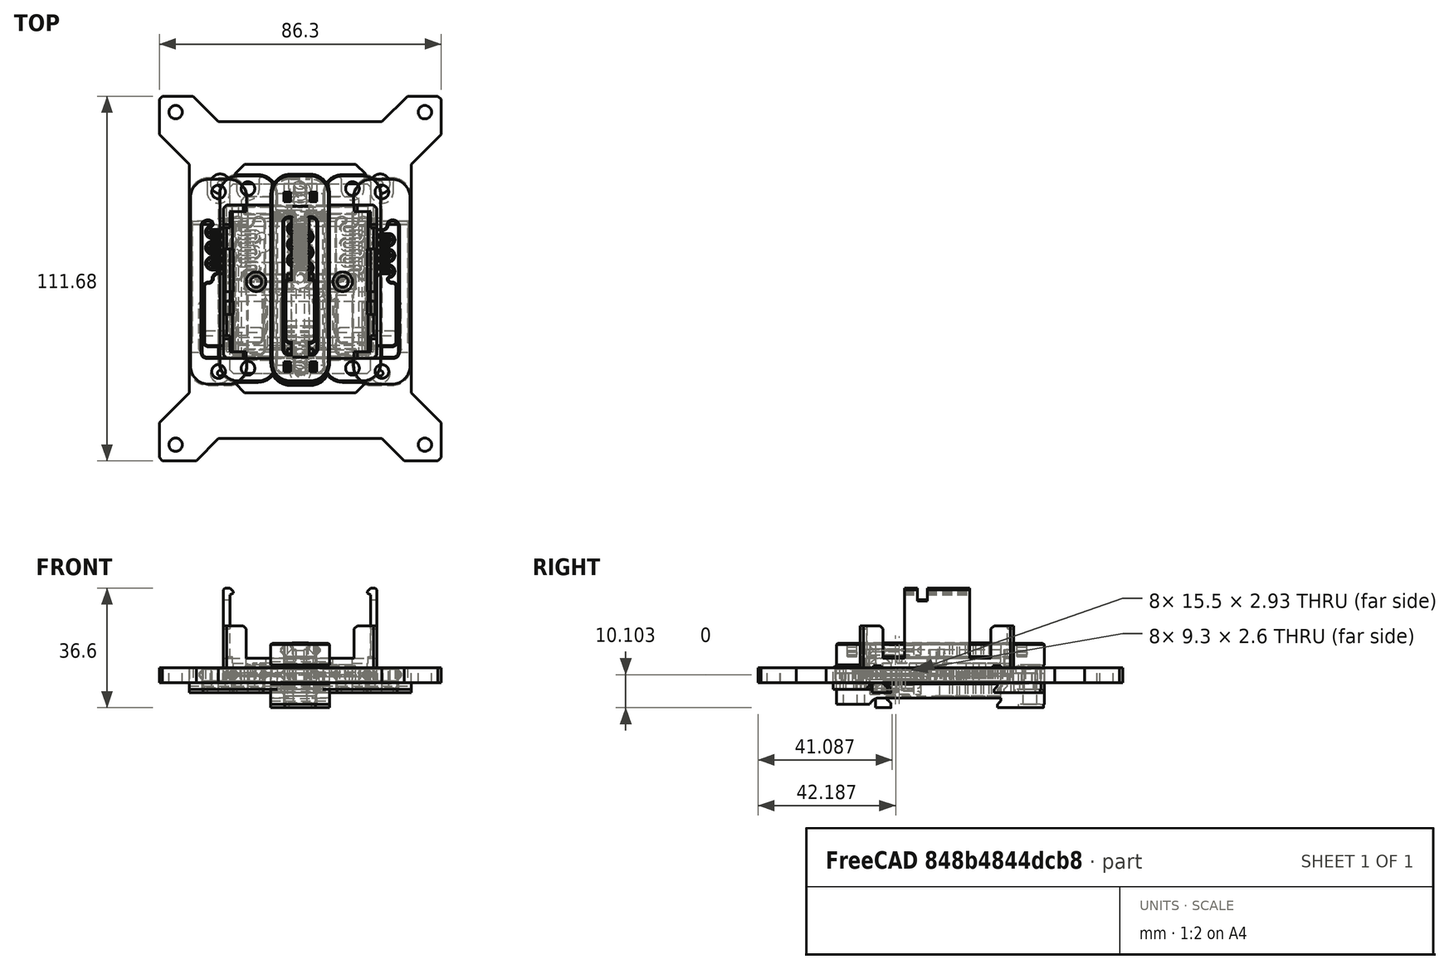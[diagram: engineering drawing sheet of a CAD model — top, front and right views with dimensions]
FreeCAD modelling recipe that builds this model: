
FCSTD DOCUMENT  (FreeCAD 0.19R24291 (Git))
Label: din-mounter
License: Other
LicenseURL: GPL3
objects: Part::Box×35, Part::Cylinder×32, Part::MultiFuse×30, Part::Cut×19, Part::Chamfer×18, Part::Feature×15, Part::Fillet×3, Sketcher::SketchObject×2, PartDesign::Pad×2, Part::MultiCommon×1, PartDesign::FeatureBase×1, PartDesign::Body×1, Part::Refine×1
note: 162 computed .brp shape members not serialized (recipe doc carries the construction recipe); baked Part::Feature solids carry a one-line shape summary decoded from their .brp

FEATURE [Part::Feature] Chamfer005007002001  label="sonoff-top "
  Placement = pos=(0,-1,7.5) rot=(0,0,1;0rad)
  shape: bbox 47 x 47 x 26.5 mm, 96 faces (baked)
FEATURE [Part::Feature] Part__Feature822  label="RS-25 PSU Bracket"
  Placement = pos=(3.35814,-1.00304,-12.0969) rot=(0,0,-1;1.5708rad)
  shape: bbox 18 x 63.6 x 7.6 mm, 163 faces (baked)
FEATURE [Part::Cylinder] Cylinder
  Angle = 360
  AttacherType = Attacher::AttachEngine3D
  Height = 6.6
  Placement = pos=(0,26.5,-6.6) rot=(0,0,1;0rad)
  Radius = 2.1
FEATURE [Part::Cylinder] Cylinder001
  Angle = 360
  AttacherType = Attacher::AttachEngine3D
  Height = 6.6
  Placement = pos=(0,-28.5,-6.6) rot=(0,0,1;0rad)
  Radius = 2.1
FEATURE [Part::MultiFuse] Fusion002
  Shapes = -> [Cylinder001,Cylinder]
FEATURE [Part::Cut] Cut  label="din-bracket-template"
  Base = -> Part__Feature822
  Placement = pos=(0,1,0) rot=(0,0,1;0rad)
  Tool = -> Fusion002
FEATURE [Part::Feature] Cut001  label="din-bracket001"
  Placement = pos=(0,1.5,4.6) rot=(0,0,1;0rad)
  shape: bbox 18 x 63.6 x 7.6 mm, 165 faces (baked)
FEATURE [Part::Box] Box  label="Cube"
  AttacherType = Attacher::AttachEngine3D
  Height = 4.6
  Length = 47
  Placement = pos=(-23.5,-24.5,0) rot=(0,0,1;0rad)
  Width = 47
FEATURE [Part::Chamfer] Chamfer
  Base = -> Box
  Edges = 4 edges r=1: [Edge1,Edge3,Edge5,Edge7]
FEATURE [Part::Chamfer] Chamfer005007002002
  Base = -> Chamfer
  Edges = 8 edges r=0.4: [Edge1,Edge5,Edge6,Edge7,Edge8,Edge9,Edge10,Edge11]
FEATURE [Part::Box] Box001  label="Cube001"
  AttacherType = Attacher::AttachEngine3D
  Height = 10
  Length = 16
  Placement = pos=(-8,-26,0) rot=(0,0,1;0rad)
  Width = 50
FEATURE [Part::Cut] Cut002
  Base = -> Chamfer005007002002
  Tool = -> Box001
FEATURE [Part::Box] Box003  label="Cube003"
  AttacherType = Attacher::AttachEngine3D
  Height = 10
  Length = 20
  Placement = pos=(-10,22.5,0) rot=(0,0,1;0rad)
  Width = 15
FEATURE [Part::Box] Box002  label="Cube002"
  AttacherType = Attacher::AttachEngine3D
  Height = 10
  Length = 20
  Placement = pos=(-10,-39.5,0) rot=(0,0,1;0rad)
  Width = 15
FEATURE [Part::MultiFuse] Fusion
  Placement = pos=(0,0,-4) rot=(0,0,1;0rad)
  Shapes = -> [Box002,Box003]
FEATURE [Part::Cut] Cut003
  Base = -> Cut001
  Tool = -> Fusion
FEATURE [Part::Chamfer] Chamfer005007002003
  Base = -> Cut003
  Edges = 2 edges r=0.4: [Edge1,Edge3]
FEATURE [Part::Chamfer] Chamfer005007002004
  Base = -> Chamfer005007002003
  Edges = 2 edges r=0.4: [Edge172,Edge174]
FEATURE [Part::MultiFuse] Fusion003
  Shapes = -> [Cut002,Chamfer005007002004]
FEATURE [Part::Cylinder] Cylinder002
  Angle = 360
  AttacherType = Attacher::AttachEngine3D
  Height = 10
  Placement = pos=(-13.5,-1,0) rot=(0,0,1;0rad)
  Radius = 2.05
FEATURE [Part::Cylinder] Cylinder003
  Angle = 360
  AttacherType = Attacher::AttachEngine3D
  Height = 10
  Placement = pos=(13,-1,0) rot=(0,0,1;0rad)
  Radius = 2.05
FEATURE [Part::MultiFuse] Fusion004
  Shapes = -> [Cylinder003,Cylinder002]
FEATURE [Part::Cut] Cut004
  Base = -> Fusion003
  Tool = -> Fusion004
FEATURE [Part::Chamfer] Chamfer005007002005  label="sonoff"
  Base = -> Cut004
  Edges = 2 edges r=0.2: [Edge19,Edge177]
FEATURE [Part::Box] Box004  label="Cube004"
  AttacherType = Attacher::AttachEngine3D
  Height = 4.6
  Length = 43
  Placement = pos=(-21.5,-29,0) rot=(0,0,1;0rad)
  Width = 58
FEATURE [Part::Cylinder] Cylinder004
  Angle = 360
  AttacherType = Attacher::AttachEngine3D
  Height = 15
  Placement = pos=(0,23.75,-6) rot=(0,0,1;0rad)
  Radius = 2.05
FEATURE [Part::Cylinder] Cylinder005
  Angle = 360
  AttacherType = Attacher::AttachEngine3D
  Height = 15
  Placement = pos=(0,-23.75,-6) rot=(0,0,1;0rad)
  Radius = 2.05
FEATURE [Part::Feature] Cut005  label="din-bracket002"
  Placement = pos=(0,3,4.6) rot=(0,0,1;0rad)
  shape: bbox 18 x 63.6 x 7.6 mm, 165 faces (baked)
FEATURE [Part::Box] Box005  label="Cube005"
  AttacherType = Attacher::AttachEngine3D
  Height = 9.6
  Length = 43
  Placement = pos=(-21.5,-29,-4) rot=(0,0,1;0rad)
  Width = 58
FEATURE [Part::MultiCommon] Common
  Shapes = -> [Box005,Cut005]
FEATURE [Part::Box] Box006  label="Cube006"
  AttacherType = Attacher::AttachEngine3D
  Height = 10
  Length = 15
  Placement = pos=(-7.5,-26.5,0) rot=(0,0,1;0rad)
  Width = 54
FEATURE [Part::Cut] Cut006
  Base = -> Box004
  Tool = -> Box006
FEATURE [Part::Box] Box007  label="Cube007"
  AttacherType = Attacher::AttachEngine3D
  Height = 6.6
  Length = 5
  Placement = pos=(-2.5,-28,-2) rot=(0,0,1;0rad)
  Width = 6
FEATURE [Part::Box] Box008  label="Cube008"
  AttacherType = Attacher::AttachEngine3D
  Height = 7.6
  Length = 10
  Placement = pos=(-5,24,-3) rot=(0,0,1;0rad)
  Width = 5
FEATURE [Part::Box] Box009  label="Cube009"
  AttacherType = Attacher::AttachEngine3D
  Height = 10
  Length = 36
  Placement = pos=(-18,-25,0) rot=(0,0,1;0rad)
  Width = 50
FEATURE [Part::MultiFuse] Fusion008
  Shapes = -> [Cylinder004,Cylinder005]
FEATURE [Part::Feature] Fusion001001  label="wago-004"
  Placement = pos=(-1,11,4.09) rot=(0,0,1;1.5708rad)
  shape: bbox 22.25 x 23.15 x 12.2 mm, 62 faces (baked)
FEATURE [Part::Feature] Fusion001002  label="wago-005"
  Placement = pos=(1,11,4.09) rot=(0,0,-1;1.5708rad)
  shape: bbox 22.25 x 23.15 x 12.2 mm, 62 faces (baked)
FEATURE [Part::Feature] Fusion001003  label="wago-006"
  Placement = pos=(1,-12,4.09) rot=(0,0,-1;1.5708rad)
  shape: bbox 22.25 x 23.15 x 12.2 mm, 62 faces (baked)
FEATURE [Part::Feature] Fusion001004  label="wago-007"
  Placement = pos=(-1,-12,4.09) rot=(0,0,1;1.5708rad)
  shape: bbox 22.25 x 23.15 x 12.2 mm, 62 faces (baked)
FEATURE [Part::MultiFuse] Fusion001005
  Placement = pos=(22,-0.5,0) rot=(0,0,1;0rad)
  Shapes = -> [Fusion001001,Fusion001004]
FEATURE [Part::MultiFuse] Fusion001006
  Placement = pos=(-22,-0.5,0) rot=(0,0,1;0rad)
  Shapes = -> [Fusion001002,Fusion001003]
FEATURE [Part::MultiFuse] Fusion001007
  Shapes = -> [Fusion001006,Fusion001005]
FEATURE [Part::Box] Box011  label="Cube011"
  AttacherType = Attacher::AttachEngine3D
  Height = 5
  Length = 18
  Placement = pos=(-9,21.8,0) rot=(0,0,1;0rad)
  Width = 9
FEATURE [Part::Box] Box012  label="Cube012"
  AttacherType = Attacher::AttachEngine3D
  Height = 5
  Length = 18
  Placement = pos=(-9,-32.8,0) rot=(0,0,1;0rad)
  Width = 9
FEATURE [Part::Fillet] Fillet
  Base = -> Box012
  Edges = 2 edges r=6: [Edge1,Edge5]
FEATURE [Part::Fillet] Fillet001
  Base = -> Box011
  Edges = 2 edges r=6: [Edge3,Edge7]
FEATURE [Part::Cylinder] Cylinder006
  Angle = 360
  AttacherType = Attacher::AttachEngine3D
  Height = 10
  Placement = pos=(0,26.5,0) rot=(0,0,1;0rad)
  Radius = 1.7
FEATURE [Part::Cylinder] Cylinder007
  Angle = 360
  AttacherType = Attacher::AttachEngine3D
  Height = 10
  Placement = pos=(0,-28.5,0) rot=(0,0,1;0rad)
  Radius = 1.7
FEATURE [Part::Cylinder] Cylinder008
  Angle = 360
  AttacherType = Attacher::AttachEngine3D
  Height = 2
  Placement = pos=(0,-28.5,0) rot=(0,0,1;0rad)
  Radius = 3.25
FEATURE [Part::Cylinder] Cylinder009
  Angle = 360
  AttacherType = Attacher::AttachEngine3D
  Height = 2
  Placement = pos=(0,26.5,0) rot=(0,0,1;0rad)
  Radius = 3.25
FEATURE [Part::MultiFuse] Fusion001008
  Shapes = -> [Cylinder007,Cylinder006]
FEATURE [Part::MultiFuse] Fusion001009
  Placement = pos=(0,0,3) rot=(0,0,1;0rad)
  Shapes = -> [Cylinder009,Cylinder008]
FEATURE [Part::MultiFuse] Fusion001010
  Shapes = -> [Fusion001009,Fusion001008]
FEATURE [Part::Chamfer] Chamfer005007002008
  Base = -> Fillet001
  Edges = 10 edges r=0.4: [Edge1,Edge4,Edge5,Edge7,Edge8,Edge9,Edge10,Edge14,Edge15,Edge16]
FEATURE [Part::Chamfer] Chamfer005007002009
  Base = -> Fillet
  Edges = 10 edges r=0.4: [Edge1,Edge4,Edge5,Edge7,Edge8,Edge9,Edge10,Edge14,Edge15,Edge16]
FEATURE [Part::MultiFuse] Fusion001011
  Shapes = -> [Chamfer005007002009,Chamfer005007002008,Fusion001007]
FEATURE [Part::Cut] Cut009  label="wago-3x4"
  Base = -> Fusion001011
  Tool = -> Fusion001010
FEATURE [Part::Chamfer] Chamfer005007002010
  Base = -> Box009
  Edges = 4 edges r=1: [Edge1,Edge3,Edge5,Edge7]
FEATURE [Part::Chamfer] Chamfer005007002011
  Base = -> Cut006
  Edges = 4 edges r=1: [Edge1,Edge3,Edge6,Edge15]
FEATURE [Part::Cut] Cut010
  Base = -> Chamfer005007002011
  Tool = -> Chamfer005007002010
FEATURE [Part::MultiFuse] Fusion001012
  Shapes = -> [Common,Box007,Box008]
FEATURE [Part::MultiFuse] Fusion001013
  Shapes = -> [Cut010,Fusion001012]
FEATURE [Part::Cut] Cut011  label="omron-ssr"
  Base = -> Fusion001013
  Tool = -> Fusion008
FEATURE [Part::Feature] Cut012  label="din-bracket-template001"
  Placement = pos=(-25,0,4.6) rot=(0,0,1;0rad)
  shape: bbox 18 x 63.6 x 7.6 mm, 165 faces (baked)
FEATURE [Part::Cylinder] Cylinder010
  Angle = 360
  AttacherType = Attacher::AttachEngine3D
  Height = 10
  Placement = pos=(38.15,50.925,0) rot=(0,0,1;0rad)
  Radius = 2.05
FEATURE [Part::Cylinder] Cylinder011
  Angle = 360
  AttacherType = Attacher::AttachEngine3D
  Height = 10
  Placement = pos=(38.15,-50.92,0) rot=(0,0,1;0rad)
  Radius = 2.05
FEATURE [Part::Cylinder] Cylinder012
  Angle = 360
  AttacherType = Attacher::AttachEngine3D
  Height = 10
  Placement = pos=(-38.15,-50.92,0) rot=(0,0,1;0rad)
  Radius = 2.05
FEATURE [Part::Cylinder] Cylinder013
  Angle = 360
  AttacherType = Attacher::AttachEngine3D
  Height = 10
  Placement = pos=(-38.15,50.925,0) rot=(0,0,1;0rad)
  Radius = 2.05
FEATURE [Part::Feature] Cut013  label="din-bracket-template002"
  Placement = pos=(25,0,4.6) rot=(0,0,1;0rad)
  shape: bbox 18 x 63.6 x 7.6 mm, 165 faces (baked)
FEATURE [Part::Box] Box013  label="Cube013"
  AttacherType = Attacher::AttachEngine3D
  Height = 4.6
  Length = 86.3
  Placement = pos=(-43.15,-55.835,0) rot=(0,0,1;0rad)
  Width = 111.67
FEATURE [Part::Box] Box014  label="Cube014"
  AttacherType = Attacher::AttachEngine3D
  Height = 10
  Length = 16
  Placement = pos=(-33,-24.5,0) rot=(0,0,1;0rad)
  Width = 44
FEATURE [Part::Box] Box015  label="Cube015"
  AttacherType = Attacher::AttachEngine3D
  Height = 10
  Length = 16
  Placement = pos=(17,-24.5,0) rot=(0,0,1;0rad)
  Width = 44
FEATURE [Part::MultiFuse] Fusion001014
  Shapes = -> [Box015,Box014]
FEATURE [Part::Cut] Cut014
  Base = -> Box013
  Tool = -> Fusion001014
FEATURE [Part::MultiFuse] Fusion001015
  Shapes = -> [Cylinder010,Cylinder011,Cylinder013,Cylinder012]
FEATURE [Part::Chamfer] Chamfer005007002012
  Base = -> Cut014
  Edges = 4 edges r=1: [Edge1,Edge3,Edge6,Edge19]
FEATURE [Part::Cut] Cut015
  Base = -> Chamfer005007002012
  Tool = -> Fusion001015
FEATURE [Part::Box] Box016  label="Cube016"
  AttacherType = Attacher::AttachEngine3D
  Height = 10
  Length = 40
  Placement = pos=(-20,-35,0) rot=(0,0,1;0rad)
  Width = 70
FEATURE [Part::Box] Box017  label="Cube017"
  AttacherType = Attacher::AttachEngine3D
  Height = 10
  Length = 70
  Placement = pos=(-35,-60,0) rot=(0,0,1;0rad)
  Width = 26
FEATURE [Part::Box] Box018  label="Cube018"
  AttacherType = Attacher::AttachEngine3D
  Height = 10
  Length = 70
  Placement = pos=(-35,55,0) rot=(0,0,1;0rad)
  Width = 26
FEATURE [Part::Chamfer] Chamfer005007002013
  Base = -> Box018
  Edges = 2 edges r=10: [Edge1,Edge5]
  Placement = pos=(0,-7,0) rot=(0,0,1;0rad)
FEATURE [Part::Chamfer] Chamfer005007002014
  Base = -> Box017
  Edges = 2 edges r=10: [Edge3,Edge7]
  Placement = pos=(0,-15,0) rot=(0,0,1;0rad)
FEATURE [Part::Chamfer] Chamfer005007002015
  Base = -> Box016
  Edges = 4 edges r=3: [Edge1,Edge3,Edge5,Edge7]
FEATURE [Part::Box] Box019  label="Cube019"
  AttacherType = Attacher::AttachEngine3D
  Height = 10
  Length = 40
  Placement = pos=(-75,-45,0) rot=(0,0,1;0rad)
  Width = 90
FEATURE [Part::Box] Box020  label="Cube020"
  AttacherType = Attacher::AttachEngine3D
  Height = 10
  Length = 40
  Placement = pos=(40,-45,0) rot=(0,0,1;0rad)
  Width = 90
FEATURE [Part::Chamfer] Chamfer005007002016
  Base = -> Box019
  Edges = 2 edges r=10: [Edge5,Edge7]
  Placement = pos=(1,0,0) rot=(0,0,1;0rad)
FEATURE [Part::Chamfer] Chamfer005007002017
  Base = -> Box020
  Edges = 2 edges r=10: [Edge1,Edge3]
  Placement = pos=(-6,0,0) rot=(0,0,1;0rad)
FEATURE [Part::MultiFuse] Fusion001016
  Shapes = -> [Chamfer005007002016,Chamfer005007002017,Chamfer005007002015,Chamfer005007002014,Chamfer005007002013]
FEATURE [Part::Box] Box021  label="Cube021"
  AttacherType = Attacher::AttachEngine3D
  Height = 4.6
  Length = 33
  Placement = pos=(-16.5,-5,0) rot=(0,0,1;0rad)
  Width = 10
FEATURE [Part::Cut] Cut016
  Base = -> Cut015
  Tool = -> Fusion001016
FEATURE [Part::MultiFuse] Fusion001017  label="skr-13_14"
  Shapes = -> [Cut016,Box021,Cut012,Cut013]
FEATURE [Part::Feature] Cut017  label="din-bracket-template003"
  Placement = pos=(-16,1,4.6) rot=(0,0,1;0rad)
  shape: bbox 18 x 63.6 x 7.6 mm, 165 faces (baked)
FEATURE [Part::Cylinder] Cylinder014
  Angle = 360
  AttacherType = Attacher::AttachEngine3D
  Height = 4.6
  Placement = pos=(24.5,29,0) rot=(0,0,1;0rad)
  Radius = 3
FEATURE [Part::Cylinder] Cylinder015
  Angle = 360
  AttacherType = Attacher::AttachEngine3D
  Height = 4.6
  Placement = pos=(24.5,-29,0) rot=(0,0,1;0rad)
  Radius = 3
FEATURE [Part::Cylinder] Cylinder016
  Angle = 360
  AttacherType = Attacher::AttachEngine3D
  Height = 4.6
  Placement = pos=(-24.5,-29,0) rot=(0,0,1;0rad)
  Radius = 3
FEATURE [Part::Cylinder] Cylinder017
  Angle = 360
  AttacherType = Attacher::AttachEngine3D
  Height = 4.6
  Placement = pos=(-24.5,29,0) rot=(0,0,1;0rad)
  Radius = 3
FEATURE [Part::Feature] Cut018  label="din-bracket-template004"
  Placement = pos=(16,1,4.6) rot=(0,0,1;0rad)
  shape: bbox 18 x 63.6 x 7.6 mm, 165 faces (baked)
FEATURE [Part::Cylinder] Cylinder018
  Angle = 360
  AttacherType = Attacher::AttachEngine3D
  Height = 4.6
  Placement = pos=(-24.5,29,0) rot=(0,0,1;0rad)
  Radius = 0.85
FEATURE [Part::Cylinder] Cylinder019
  Angle = 360
  AttacherType = Attacher::AttachEngine3D
  Height = 4.6
  Placement = pos=(24.5,29,0) rot=(0,0,1;0rad)
  Radius = 0.85
FEATURE [Part::Cylinder] Cylinder020
  Angle = 360
  AttacherType = Attacher::AttachEngine3D
  Height = 4.6
  Placement = pos=(24.5,-29,0) rot=(0,0,1;0rad)
  Radius = 0.85
FEATURE [Part::Cylinder] Cylinder021
  Angle = 360
  AttacherType = Attacher::AttachEngine3D
  Height = 4.6
  Placement = pos=(-24.5,-29,0) rot=(0,0,1;0rad)
  Radius = 0.85
FEATURE [Part::MultiFuse] Fusion001018
  Shapes = -> [Cylinder021,Cylinder020,Cylinder019,Cylinder018]
FEATURE [Part::MultiFuse] Fusion001019
  Shapes = -> [Cylinder017,Cylinder014,Cylinder015,Cylinder016]
FEATURE [Part::Box] Box022  label="Cube022"
  AttacherType = Attacher::AttachEngine3D
  Height = 4.6
  Length = 15
  Placement = pos=(-7.5,-26.5,0) rot=(0,0,1;0rad)
  Width = 5
FEATURE [Part::Box] Box023  label="Cube023"
  AttacherType = Attacher::AttachEngine3D
  Height = 4.6
  Length = 15
  Placement = pos=(-7.5,21,0) rot=(0,0,1;0rad)
  Width = 5
FEATURE [Part::MultiFuse] Fusion001020
  Shapes = -> [Box023,Box022,Cut018,Cut017,Fusion001019]
FEATURE [Part::Cut] Cut019  label="pi"
  Base = -> Fusion001020
  Tool = -> Fusion001018
FEATURE [Part::Cylinder] Cylinder022
  Angle = 360
  AttacherType = Attacher::AttachEngine3D
  Height = 4
  Radius = 3
FEATURE [Part::Cylinder] Cylinder023
  Angle = 360
  AttacherType = Attacher::AttachEngine3D
  Height = 4
  Radius = 1.2
FEATURE [Part::Cut] Cut020  label="m2-washer"
  Base = -> Cylinder022
  Tool = -> Cylinder023
FEATURE [Part::Cylinder] Cylinder024
  Angle = 360
  AttacherType = Attacher::AttachEngine3D
  Height = 4
  Radius = 3.5
FEATURE [Part::Cylinder] Cylinder025
  Angle = 360
  AttacherType = Attacher::AttachEngine3D
  Height = 10
  Radius = 1.7
FEATURE [Part::Cut] Cut021  label="m3-washer"
  Base = -> Cylinder024
  Tool = -> Cylinder025
FEATURE [Part::Box] Box024  label="Cube024"
  AttacherType = Attacher::AttachEngine3D
  Height = 8
  Length = 45
  Placement = pos=(-22.5,-22.5,0) rot=(0,0,1;0rad)
  Width = 45
FEATURE [Part::Box] Box025  label="Cube025"
  AttacherType = Attacher::AttachEngine3D
  Height = 6
  Length = 41
  Placement = pos=(-20.5,-22.5,3) rot=(0,0,1;0rad)
  Width = 45
FEATURE [Part::Cylinder] Cylinder026
  Angle = 360
  AttacherType = Attacher::AttachEngine3D
  Height = 6
  Placement = pos=(-11.5,11,0) rot=(0,0,1;0rad)
  Radius = 0.85
FEATURE [Part::Cylinder] Cylinder027
  Angle = 360
  AttacherType = Attacher::AttachEngine3D
  Height = 6
  Placement = pos=(6.645,-6.415,0) rot=(0,0,1;0rad)
  Radius = 0.85
FEATURE [Part::Box] Box026  label="Cube026"
  AttacherType = Attacher::AttachEngine3D
  Height = 3
  Length = 18
  Placement = pos=(-9,22.5,0) rot=(0,0,1;0rad)
  Width = 9.4
FEATURE [Part::Box] Box027  label="Cube027"
  AttacherType = Attacher::AttachEngine3D
  Height = 3
  Length = 18
  Placement = pos=(-9,-31.9,0) rot=(0,0,1;0rad)
  Width = 9.4
FEATURE [Part::MultiFuse] Fusion001021
  Shapes = -> [Box027,Box026]
FEATURE [Part::Fillet] Fillet002
  Base = -> Fusion001021
  Edges = 4 edges r=6: [Edge1,Edge5,Edge15,Edge19]
FEATURE [Part::MultiFuse] Fusion001022
  Shapes = -> [Box024,Fillet002]
FEATURE [Part::Cut] Cut022
  Base = -> Fusion001022
  Tool = -> Box025
FEATURE [Part::Cylinder] Cylinder028
  Angle = 360
  AttacherType = Attacher::AttachEngine3D
  Height = 6
  Placement = pos=(-11.5,11,0) rot=(0,0,1;0rad)
  Radius = 3
FEATURE [Part::Cylinder] Cylinder029
  Angle = 360
  AttacherType = Attacher::AttachEngine3D
  Height = 6
  Placement = pos=(6.645,-6.415,0) rot=(0,0,1;0rad)
  Radius = 3
FEATURE [Part::Cylinder] Cylinder030
  Angle = 360
  AttacherType = Attacher::AttachEngine3D
  Height = 10
  Placement = pos=(0,27.5,0) rot=(0,0,1;0rad)
  Radius = 1.7
FEATURE [Part::Cylinder] Cylinder031
  Angle = 360
  AttacherType = Attacher::AttachEngine3D
  Height = 10
  Placement = pos=(0,-27.5,0) rot=(0,0,1;0rad)
  Radius = 1.7
FEATURE [Part::MultiFuse] Fusion001026
  Shapes = -> [Cylinder031,Cylinder030]
FEATURE [Part::Cut] Cut023
  Base = -> Cut022
  Tool = -> Fusion001026
FEATURE [Part::Box] Box028  label="Cube028"
  AttacherType = Attacher::AttachEngine3D
  Height = 6
  Length = 5
  Placement = pos=(-21,-22.5,0) rot=(0,0,1;0rad)
  Width = 5
FEATURE [Part::Box] Box029  label="Cube029"
  AttacherType = Attacher::AttachEngine3D
  Height = 6
  Length = 5
  Placement = pos=(16,-22.5,0) rot=(0,0,1;0rad)
  Width = 5
FEATURE [Part::Box] Box030  label="Cube030"
  AttacherType = Attacher::AttachEngine3D
  Height = 6
  Length = 5
  Placement = pos=(16,17.5,0) rot=(0,0,1;0rad)
  Width = 5
FEATURE [Part::Box] Box031  label="Cube031"
  AttacherType = Attacher::AttachEngine3D
  Height = 6
  Length = 5
  Placement = pos=(-21,17.5,0) rot=(0,0,1;0rad)
  Width = 5
FEATURE [Part::MultiFuse] Fusion001030
  Shapes = -> [Box030,Box031,Box029,Box028]
FEATURE [Part::Box] Box032  label="Cube032"
  AttacherType = Attacher::AttachEngine3D
  Height = 10
  Length = 41.5
  Placement = pos=(-20.75,-22.5,6) rot=(0,0,1;0rad)
  Width = 45
FEATURE [Part::MultiFuse] Fusion001031
  Shapes = -> [Cut023,Fusion001030]
FEATURE [Part::Cut] Cut024
  Base = -> Fusion001031
  Tool = -> Box032
FEATURE [Part::MultiFuse] Fusion001032
  Shapes = -> [Cylinder029,Cylinder028,Cut024]
FEATURE [Part::MultiFuse] Fusion001033
  Shapes = -> [Cylinder027,Cylinder026]
FEATURE [Part::Cut] Cut025
  Base = -> Fusion001032
  Tool = -> Fusion001033
FEATURE [Part::Feature] Part__Feature823  label="RS-25 PSU Bracket001"
  Placement = pos=(3.35814,-1.00304,-12.0969) rot=(0,0,-1;1.5708rad)
  shape: bbox 18 x 63.6 x 7.6 mm, 163 faces (baked)
FEATURE [PartDesign::FeatureBase] BaseFeature
  BaseFeature = -> Part__Feature823
FEATURE [Sketcher::SketchObject] Sketch
  FullyConstrained = false
  MapMode = 5
  Placement = pos=(-1.08e-14,0,12.1) rot=(0,0,1;0rad)
  Support = -> [BaseFeature]
  sketch-geometry (1):
    g0: Circle CenterX=-27.4396 CenterY=-3.37328 CenterZ=0 NormalX=0 NormalY=0 NormalZ=1 AngleXU=0 Radius=2.66302
FEATURE [PartDesign::Pad] Pad
  BaseFeature = -> BaseFeature
  Direction = (1,1,1)
  Length = 10
  Length2 = 100
  Profile = -> Sketch
  Type = 3
  UpToFace = -> BaseFeature [Face161]
FEATURE [Sketcher::SketchObject] Sketch001
  FullyConstrained = false
  MapMode = 5
  Placement = pos=(-1.08e-14,0,12.1) rot=(0,0,1;0rad)
  Support = -> [Pad]
  sketch-geometry (1):
    g0: Circle CenterX=27.4966 CenterY=-3.39954 CenterZ=0 NormalX=0 NormalY=0 NormalZ=1 AngleXU=0 Radius=2.31774
FEATURE [PartDesign::Pad] Pad001
  BaseFeature = -> Pad
  Direction = (1,1,1)
  Length = 10
  Length2 = 100
  Profile = -> Sketch001
  Type = 3
  UpToFace = -> Pad [Face132]
FEATURE [PartDesign::Body] Body
  BaseFeature = -> Part__Feature823
  Group = -> [BaseFeature,Sketch,Pad,Sketch001,Pad001]
  Origin = -> Origin
  Placement = pos=(3.36,-7e-16,0) rot=(0,0,1;4.71239rad)
  Tip = -> Pad001
FEATURE [Part::Box] Box033  label="Cube033"
  AttacherType = Attacher::AttachEngine3D
  Height = 5
  Length = 2
  Placement = pos=(-5,0,0) rot=(0,0,1;0rad)
  Width = 3
FEATURE [Part::Box] Box034  label="Cube034"
  AttacherType = Attacher::AttachEngine3D
  Height = 2
  Length = 6
  Placement = pos=(-3,0,0) rot=(0,0,1;0rad)
  Width = 3
FEATURE [Part::Box] Box035  label="Cube035"
  AttacherType = Attacher::AttachEngine3D
  Height = 5
  Length = 2
  Placement = pos=(3,0,0) rot=(0,0,1;0rad)
  Width = 3
FEATURE [Part::MultiFuse] Fusion001034
  Shapes = -> [Box033,Box034,Box035]
FEATURE [Part::Chamfer] Chamfer005007002018
  Base = -> Fusion001034
  Edges = 2 edges r=1: [Edge4,Edge32]
FEATURE [Part::Chamfer] Chamfer005007002019
  Base = -> Chamfer005007002018
  Edges = 2 edges r=1: [Edge21,Edge31]
FEATURE [Part::Chamfer] Chamfer005007002020
  Base = -> Chamfer005007002019
  Edges = 4 edges r=0.5: [Edge19,Edge22,Edge46,Edge49]
  Placement = pos=(0,23.5,8) rot=(0,0,1;0rad)
FEATURE [Part::Feature] Chamfer005007002020001
  Placement = pos=(0,-28.5,8) rot=(0,0,1;0rad)
  shape: bbox 10 x 3 x 5 mm, 24 faces (baked)
FEATURE [Part::MultiFuse] Fusion001035
  Shapes = -> [Chamfer005007002020001,Chamfer005007002020]
FEATURE [Part::Refine] Body001
  Source = -> Body
FEATURE [Part::Cut] Cut026
  Base = -> Body001
  Tool = -> Fusion001035
FEATURE [Part::Feature] Cut026001
  shape: bbox 18 x 63.6 x 7.6 mm, 203 faces (baked)
